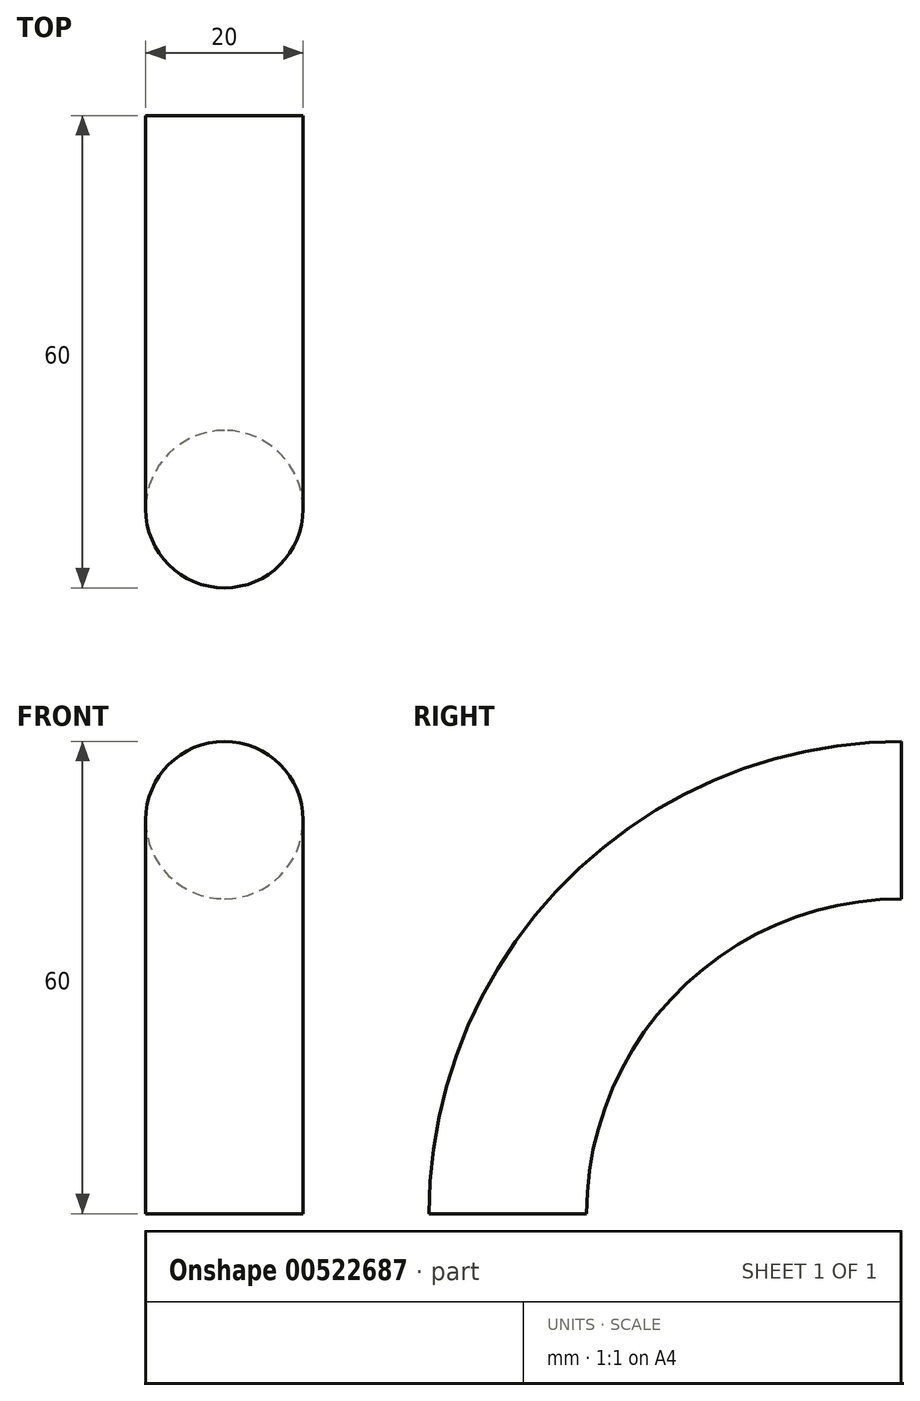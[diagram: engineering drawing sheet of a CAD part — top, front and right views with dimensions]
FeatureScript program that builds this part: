
annotation { "Feature Type Name" : "Feature", "Feature Type Description" : "" }
export const myFeature = defineFeature(function(context is Context, id is Id, definition is map)
    precondition{}
    {
        {
            var Q0;
            Q0=qCreatedBy(makeId("Right.planeOp"),FACE);
            var sketch = newSketch(context, id + "F0", { "sketchPlane" : qUnion([Q0])});
            skArc(sketch, "E0", {"start": v(0, 50) * mm, "mid": v(-35.36, 35.36) * mm, "end": v(-50, 0) * mm});
            skSolve(sketch);
        }
        {
            var Q0;
            Q0=qCreatedBy(makeId("Front.planeOp"),FACE);
            var sketch = newSketch(context, id + "F1", { "sketchPlane" : qUnion([Q0])});
            skCircle(sketch, "E1", {"center": v(0, 50) * mm, "radius": 10 * mm});
            skSolve(sketch);
        }
        {
            var Q0;
            Q0=makeQuery(id+"F1.imprint","IMPRINT",FACE,{"disambiguationData":[TD([[makeQuery(id+"F1.imprint","IMPRINT",EDGE,{"derivedFrom":sQuery(id+"F1.wireOp",EDGE,"E1")}),1.0]])]});
            var Q1;
            Q1=sQuery(id+"F0.wireOp",EDGE,"E0");
            sweep(context, id + "F2", {"profiles" : qUnion([Q0]), "path" : qUnion([Q1])});
        }
    });
